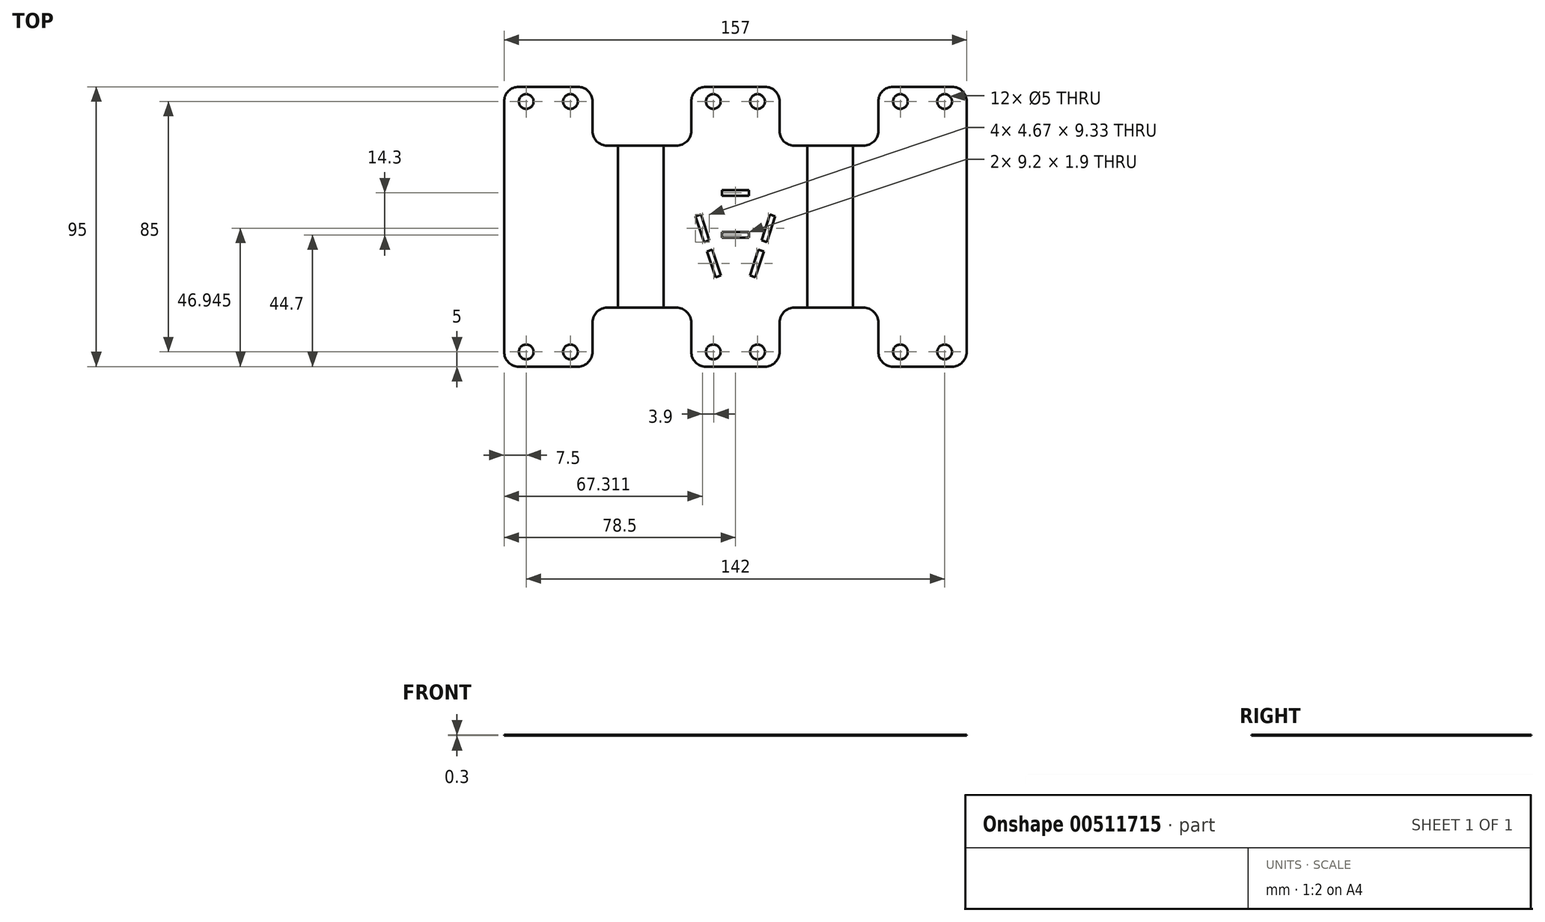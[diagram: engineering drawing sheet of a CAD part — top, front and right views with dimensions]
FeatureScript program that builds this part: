
annotation { "Feature Type Name" : "Feature", "Feature Type Description" : "" }
export const myFeature = defineFeature(function(context is Context, id is Id, definition is map)
    precondition{}
    {
        {
            var Q0;
            Q0=qCreatedBy(makeId("Top.planeOp"),FACE);
            var sketch = newSketch(context, id + "F0", { "sketchPlane" : qUnion([Q0])});
            skLineSegment(sketch, "E0.bottom", {"start": v(-15, 47.5) * mm, "end": v(15, 47.5) * mm});
            skLineSegment(sketch, "E0.top", {"start": v(-15, -47.5) * mm, "end": v(15, -47.5) * mm});
            skLineSegment(sketch, "E0.left", {"start": v(-15, 47.5) * mm, "end": v(-15, 27.5) * mm});
            skLineSegment(sketch, "E0.right", {"start": v(15, 47.5) * mm, "end": v(15, 27.5) * mm});
            skLineSegment(sketch, "E1.bottom", {"start": v(48.5, 47.5) * mm, "end": v(78.5, 47.5) * mm});
            skLineSegment(sketch, "E1.top", {"start": v(48.5, -47.5) * mm, "end": v(78.5, -47.5) * mm});
            skLineSegment(sketch, "E1.left", {"start": v(48.5, 47.5) * mm, "end": v(48.5, 27.5) * mm});
            skLineSegment(sketch, "E1.right", {"start": v(78.5, 47.5) * mm, "end": v(78.5, -47.5) * mm});
            skLineSegment(sketch, "E2.bottom", {"start": v(-48.5, 47.5) * mm, "end": v(-78.5, 47.5) * mm});
            skLineSegment(sketch, "E2.top", {"start": v(-48.5, -47.5) * mm, "end": v(-78.5, -47.5) * mm});
            skLineSegment(sketch, "E2.left", {"start": v(-48.5, 47.5) * mm, "end": v(-48.5, 27.5) * mm});
            skLineSegment(sketch, "E2.right", {"start": v(-78.5, 47.5) * mm, "end": v(-78.5, -47.5) * mm});
            skLineSegment(sketch, "E3.bottom", {"start": v(-48.5, 27.5) * mm, "end": v(-15, 27.5) * mm});
            skLineSegment(sketch, "E3.top", {"start": v(-48.5, -27.5) * mm, "end": v(-15, -27.5) * mm});
            skLineSegment(sketch, "E4.bottom", {"start": v(15, -27.5) * mm, "end": v(48.5, -27.5) * mm});
            skLineSegment(sketch, "E4.top", {"start": v(15, 27.5) * mm, "end": v(48.5, 27.5) * mm});
            skLineSegment(sketch, "E5.trimOffspring", {"start": v(-48.5, -27.5) * mm, "end": v(-48.5, -47.5) * mm});
            skLineSegment(sketch, "E6.trimOffspring", {"start": v(-15, -27.5) * mm, "end": v(-15, -47.5) * mm});
            skLineSegment(sketch, "E7.trimOffspring", {"start": v(15, -27.5) * mm, "end": v(15, -47.5) * mm});
            skLineSegment(sketch, "E8.trimOffspring", {"start": v(48.5, -27.5) * mm, "end": v(48.5, -47.5) * mm});
            skCircle(sketch, "E9", {"center": v(-7.5, 42.5) * mm, "radius": 2.5 * mm});
            skCircle(sketch, "E10", {"center": v(7.5, 42.5) * mm, "radius": 2.5 * mm});
            skCircle(sketch, "E11", {"center": v(-7.5, -42.5) * mm, "radius": 2.5 * mm});
            skCircle(sketch, "E12", {"center": v(7.5, -42.5) * mm, "radius": 2.5 * mm});
            skCircle(sketch, "E13", {"center": v(-56, 42.5) * mm, "radius": 2.5 * mm});
            skCircle(sketch, "E14", {"center": v(-71, 42.5) * mm, "radius": 2.5 * mm});
            skCircle(sketch, "E15", {"center": v(-56, -42.5) * mm, "radius": 2.5 * mm});
            skCircle(sketch, "E16", {"center": v(-71, -42.5) * mm, "radius": 2.5 * mm});
            skCircle(sketch, "E17", {"center": v(56, -42.5) * mm, "radius": 2.5 * mm});
            skCircle(sketch, "E18", {"center": v(71, -42.5) * mm, "radius": 2.5 * mm});
            skCircle(sketch, "E19", {"center": v(71, 42.5) * mm, "radius": 2.5 * mm});
            skCircle(sketch, "E20", {"center": v(56, 42.5) * mm, "radius": 2.5 * mm});
            skSolve(sketch);
        }
        {
            var Q0;
            Q0 = qSketchRegion(id + "F0", true);
            extrude(context, id + "F1", {"entities" : qUnion([Q0]), "depth" : 25 * mm});
        }
        {
            var Q0;
            Q0 = qSketchRegion(id + "F0", true);
            extrude(context, id + "F2", {"entities" : qUnion([Q0]), "operationType" : NewBodyOperationType.REMOVE, "oppositeDirection" : true, "depth" : 25 * mm});
        }
        {
            var Q0;
            Q0=makeQuery(id+"F1.opExtrude","CAP_FACE",FACE,{"disambiguationData":[OSD([sQuery(id+"F0.wireOp",EDGE,"E0.bottom"),sQuery(id+"F0.wireOp",EDGE,"E0.top"),sQuery(id+"F0.wireOp",EDGE,"E0.left"),sQuery(id+"F0.wireOp",EDGE,"E0.right"),sQuery(id+"F0.wireOp",EDGE,"E1.bottom"),sQuery(id+"F0.wireOp",EDGE,"E1.top"),sQuery(id+"F0.wireOp",EDGE,"E1.left"),sQuery(id+"F0.wireOp",EDGE,"E1.right"),sQuery(id+"F0.wireOp",EDGE,"E2.bottom"),sQuery(id+"F0.wireOp",EDGE,"E2.top"),sQuery(id+"F0.wireOp",EDGE,"E2.left"),sQuery(id+"F0.wireOp",EDGE,"E2.right"),sQuery(id+"F0.wireOp",EDGE,"E3.bottom"),sQuery(id+"F0.wireOp",EDGE,"E3.top"),sQuery(id+"F0.wireOp",EDGE,"E4.bottom"),sQuery(id+"F0.wireOp",EDGE,"E4.top"),sQuery(id+"F0.wireOp",EDGE,"E5.trimOffspring"),sQuery(id+"F0.wireOp",EDGE,"E6.trimOffspring"),sQuery(id+"F0.wireOp",EDGE,"E7.trimOffspring"),sQuery(id+"F0.wireOp",EDGE,"E8.trimOffspring"),sQuery(id+"F0.wireOp",EDGE,"E9"),sQuery(id+"F0.wireOp",EDGE,"E10"),sQuery(id+"F0.wireOp",EDGE,"E11"),sQuery(id+"F0.wireOp",EDGE,"E12"),sQuery(id+"F0.wireOp",EDGE,"E13"),sQuery(id+"F0.wireOp",EDGE,"E14"),sQuery(id+"F0.wireOp",EDGE,"E15"),sQuery(id+"F0.wireOp",EDGE,"E16"),sQuery(id+"F0.wireOp",EDGE,"E17"),sQuery(id+"F0.wireOp",EDGE,"E18"),sQuery(id+"F0.wireOp",EDGE,"E19"),sQuery(id+"F0.wireOp",EDGE,"E20")])],"isStart":false});
            var sketch = newSketch(context, id + "F3", { "sketchPlane" : qUnion([Q0])});
            skLineSegment(sketch, "E21.bottom", {"start": v(-4.6, 12.45) * mm, "end": v(4.6, 12.45) * mm});
            skLineSegment(sketch, "E21.top", {"start": v(-4.6, 10.55) * mm, "end": v(4.6, 10.55) * mm});
            skLineSegment(sketch, "E21.left", {"start": v(-4.6, 12.45) * mm, "end": v(-4.6, 10.55) * mm});
            skLineSegment(sketch, "E21.right", {"start": v(4.6, 12.45) * mm, "end": v(4.6, 10.55) * mm});
            skLineSegment(sketch, "E22.bottom", {"start": v(-4.6, -3.75) * mm, "end": v(4.6, -3.75) * mm});
            skLineSegment(sketch, "E22.top", {"start": v(-4.6, -1.85) * mm, "end": v(4.6, -1.85) * mm});
            skLineSegment(sketch, "E22.left", {"start": v(-4.6, -3.75) * mm, "end": v(-4.6, -1.85) * mm});
            skLineSegment(sketch, "E22.right", {"start": v(4.6, -3.75) * mm, "end": v(4.6, -1.85) * mm});
            skLineSegment(sketch, "E23", {"start": v(-11.72, 4.11) * mm, "end": v(-8.85, -4.63) * mm});
            skLineSegment(sketch, "E24", {"start": v(-4.95, -16.53) * mm, "end": v(-6.76, -17.12) * mm});
            skLineSegment(sketch, "E25", {"start": v(-6.76, -17.12) * mm, "end": v(-9.62, -8.38) * mm});
            skLineSegment(sketch, "E26", {"start": v(-13.52, 3.52) * mm, "end": v(-11.72, 4.11) * mm});
            skLineSegment(sketch, "E27", {"start": v(11.72, 4.11) * mm, "end": v(8.85, -4.63) * mm});
            skLineSegment(sketch, "E28", {"start": v(4.95, -16.53) * mm, "end": v(6.76, -17.12) * mm});
            skLineSegment(sketch, "E29", {"start": v(6.76, -17.12) * mm, "end": v(9.62, -8.38) * mm});
            skLineSegment(sketch, "E30", {"start": v(13.52, 3.52) * mm, "end": v(11.72, 4.11) * mm});
            skLineSegment(sketch, "E31", {"start": v(-10.66, -5.22) * mm, "end": v(-8.85, -4.63) * mm});
            skLineSegment(sketch, "E32", {"start": v(-9.62, -8.38) * mm, "end": v(-7.82, -7.79) * mm});
            skLineSegment(sketch, "E33", {"start": v(8.85, -4.63) * mm, "end": v(10.66, -5.22) * mm});
            skLineSegment(sketch, "E34", {"start": v(7.82, -7.79) * mm, "end": v(9.62, -8.38) * mm});
            skLineSegment(sketch, "E35.trimOffspring", {"start": v(10.66, -5.22) * mm, "end": v(13.52, 3.52) * mm});
            skLineSegment(sketch, "E36.trimOffspring", {"start": v(7.82, -7.79) * mm, "end": v(4.95, -16.53) * mm});
            skLineSegment(sketch, "E37.trimOffspring", {"start": v(-7.82, -7.79) * mm, "end": v(-4.95, -16.53) * mm});
            skLineSegment(sketch, "E38.trimOffspring", {"start": v(-10.66, -5.22) * mm, "end": v(-13.52, 3.52) * mm});
            skSolve(sketch);
        }
        {
            var Q0;
            Q0 = qSketchRegion(id + "F3", true);
            extrude(context, id + "F4", {"entities" : qUnion([Q0]), "operationType" : NewBodyOperationType.REMOVE, "oppositeDirection" : true, "depth" : 25 * mm});
        }
        {
            var Q0;
            Q0=makeQuery(id+"F1.opExtrude","SWEPT_EDGE",EDGE,{"disambiguationData":[OSD([sQuery(id+"F0.wireOp",EDGE,"E2.bottom"),sQuery(id+"F0.wireOp",EDGE,"E2.left")])]});
            var Q1;
            Q1=makeQuery(id+"F1.opExtrude","SWEPT_EDGE",EDGE,{"disambiguationData":[OSD([sQuery(id+"F0.wireOp",EDGE,"E2.left"),sQuery(id+"F0.wireOp",EDGE,"E3.bottom")])]});
            var Q2;
            Q2=makeQuery(id+"F1.opExtrude","SWEPT_EDGE",EDGE,{"disambiguationData":[OSD([sQuery(id+"F0.wireOp",EDGE,"E0.bottom"),sQuery(id+"F0.wireOp",EDGE,"E0.right")])]});
            var Q3;
            Q3=makeQuery(id+"F1.opExtrude","SWEPT_EDGE",EDGE,{"disambiguationData":[OSD([sQuery(id+"F0.wireOp",EDGE,"E0.right"),sQuery(id+"F0.wireOp",EDGE,"E4.top")])]});
            var Q4;
            Q4=makeQuery(id+"F1.opExtrude","SWEPT_EDGE",EDGE,{"disambiguationData":[OSD([sQuery(id+"F0.wireOp",EDGE,"E1.bottom"),sQuery(id+"F0.wireOp",EDGE,"E1.right")])]});
            var Q5;
            Q5=makeQuery(id+"F1.opExtrude","SWEPT_EDGE",EDGE,{"disambiguationData":[OSD([sQuery(id+"F0.wireOp",EDGE,"E1.bottom"),sQuery(id+"F0.wireOp",EDGE,"E1.left")])]});
            var Q6;
            Q6=makeQuery(id+"F1.opExtrude","SWEPT_EDGE",EDGE,{"disambiguationData":[OSD([sQuery(id+"F0.wireOp",EDGE,"E0.bottom"),sQuery(id+"F0.wireOp",EDGE,"E0.left")])]});
            var Q7;
            Q7=makeQuery(id+"F1.opExtrude","SWEPT_EDGE",EDGE,{"disambiguationData":[OSD([sQuery(id+"F0.wireOp",EDGE,"E1.left"),sQuery(id+"F0.wireOp",EDGE,"E4.top")])]});
            var Q8;
            Q8=makeQuery(id+"F1.opExtrude","SWEPT_EDGE",EDGE,{"disambiguationData":[OSD([sQuery(id+"F0.wireOp",EDGE,"E0.left"),sQuery(id+"F0.wireOp",EDGE,"E3.bottom")])]});
            var Q9;
            Q9=makeQuery(id+"F1.opExtrude","SWEPT_EDGE",EDGE,{"disambiguationData":[OSD([sQuery(id+"F0.wireOp",EDGE,"E2.bottom"),sQuery(id+"F0.wireOp",EDGE,"E2.right")])]});
            var Q10;
            Q10=makeQuery(id+"F1.opExtrude","SWEPT_EDGE",EDGE,{"disambiguationData":[OSD([sQuery(id+"F0.wireOp",EDGE,"E4.bottom"),sQuery(id+"F0.wireOp",EDGE,"E7.trimOffspring")])]});
            var Q11;
            Q11=makeQuery(id+"F1.opExtrude","SWEPT_EDGE",EDGE,{"disambiguationData":[OSD([sQuery(id+"F0.wireOp",EDGE,"E0.top"),sQuery(id+"F0.wireOp",EDGE,"E7.trimOffspring")])]});
            var Q12;
            Q12=makeQuery(id+"F1.opExtrude","SWEPT_EDGE",EDGE,{"disambiguationData":[OSD([sQuery(id+"F0.wireOp",EDGE,"E1.top"),sQuery(id+"F0.wireOp",EDGE,"E1.right")])]});
            var Q13;
            Q13=makeQuery(id+"F1.opExtrude","SWEPT_EDGE",EDGE,{"disambiguationData":[OSD([sQuery(id+"F0.wireOp",EDGE,"E3.top"),sQuery(id+"F0.wireOp",EDGE,"E5.trimOffspring")])]});
            var Q14;
            Q14=makeQuery(id+"F1.opExtrude","SWEPT_EDGE",EDGE,{"disambiguationData":[OSD([sQuery(id+"F0.wireOp",EDGE,"E2.top"),sQuery(id+"F0.wireOp",EDGE,"E5.trimOffspring")])]});
            var Q15;
            Q15=makeQuery(id+"F1.opExtrude","SWEPT_EDGE",EDGE,{"disambiguationData":[OSD([sQuery(id+"F0.wireOp",EDGE,"E4.bottom"),sQuery(id+"F0.wireOp",EDGE,"E8.trimOffspring")])]});
            var Q16;
            Q16=makeQuery(id+"F1.opExtrude","SWEPT_EDGE",EDGE,{"disambiguationData":[OSD([sQuery(id+"F0.wireOp",EDGE,"E1.top"),sQuery(id+"F0.wireOp",EDGE,"E8.trimOffspring")])]});
            var Q17;
            Q17=makeQuery(id+"F1.opExtrude","SWEPT_EDGE",EDGE,{"disambiguationData":[OSD([sQuery(id+"F0.wireOp",EDGE,"E3.top"),sQuery(id+"F0.wireOp",EDGE,"E6.trimOffspring")])]});
            var Q18;
            Q18=makeQuery(id+"F1.opExtrude","SWEPT_EDGE",EDGE,{"disambiguationData":[OSD([sQuery(id+"F0.wireOp",EDGE,"E0.top"),sQuery(id+"F0.wireOp",EDGE,"E6.trimOffspring")])]});
            var Q19;
            Q19=makeQuery(id+"F1.opExtrude","SWEPT_EDGE",EDGE,{"disambiguationData":[OSD([sQuery(id+"F0.wireOp",EDGE,"E2.top"),sQuery(id+"F0.wireOp",EDGE,"E2.right")])]});
            fillet(context, id + "F5", {"entities" : qUnion([Q0, Q1, Q2, Q3, Q4, Q5, Q6, Q7, Q8, Q9, Q10, Q11, Q12, Q13, Q14, Q15, Q16, Q17, Q18, Q19]), "radius" : 5 * mm, "tangentPropagation" : true, "allowEdgeOverflow" : false});
        }
        {
            var Q0;
            Q0=qCreatedBy(makeId("Front.planeOp"),FACE);
            var sketch = newSketch(context, id + "F6", { "sketchPlane" : qUnion([Q0])});
            skLineSegment(sketch, "E39", {"start": v(-40.85, 32.5) * mm, "end": v(-38.85, 32.5) * mm});
            skLineSegment(sketch, "E40", {"start": v(-40.85, 32.5) * mm, "end": v(-39.85, 24.9) * mm});
            skLineSegment(sketch, "E41", {"start": v(-39.85, 24.9) * mm, "end": v(-38.85, 32.5) * mm});
            skLineSegment(sketch, "E42", {"start": v(-25.35, 32.5) * mm, "end": v(-24.35, 24.9) * mm});
            skLineSegment(sketch, "E43", {"start": v(-24.35, 24.9) * mm, "end": v(-23.35, 32.5) * mm});
            skLineSegment(sketch, "E44", {"start": v(40.85, 32.5) * mm, "end": v(39.85, 24.9) * mm});
            skLineSegment(sketch, "E45", {"start": v(39.85, 24.9) * mm, "end": v(38.85, 32.5) * mm});
            skLineSegment(sketch, "E46", {"start": v(25.35, 32.5) * mm, "end": v(24.35, 24.9) * mm});
            skLineSegment(sketch, "E47", {"start": v(24.35, 24.9) * mm, "end": v(23.35, 32.5) * mm});
            skLineSegment(sketch, "E48.trimOffspring", {"start": v(-25.35, 32.5) * mm, "end": v(-23.35, 32.5) * mm});
            skLineSegment(sketch, "E49.trimOffspring", {"start": v(23.35, 32.5) * mm, "end": v(25.35, 32.5) * mm});
            skLineSegment(sketch, "E50.trimOffspring", {"start": v(38.85, 32.5) * mm, "end": v(40.85, 32.5) * mm});
            skSolve(sketch);
        }
        {
            var Q0;
            {var subQ0=sQuery(id+"F6.wireOp",EDGE,"E40");Q0=makeQuery(id+"F6.imprint","IMPRINT",FACE,{"disambiguationData":[TD([[makeQuery(id+"F6.imprint","IMPRINT",EDGE,{"derivedFrom":subQ0}),1.0]])]});}
            var Q1;
            {var subQ0=sQuery(id+"F6.wireOp",EDGE,"E44");Q1=makeQuery(id+"F6.imprint","IMPRINT",FACE,{"disambiguationData":[TD([[makeQuery(id+"F6.imprint","IMPRINT",EDGE,{"derivedFrom":subQ0}),-1.0]])]});}
            var Q2;
            {var subQ0=sQuery(id+"F6.wireOp",EDGE,"E42");Q2=makeQuery(id+"F6.imprint","IMPRINT",FACE,{"disambiguationData":[TD([[makeQuery(id+"F6.imprint","IMPRINT",EDGE,{"derivedFrom":subQ0}),1.0]])]});}
            var Q3;
            {var subQ0=sQuery(id+"F6.wireOp",EDGE,"E46");Q3=makeQuery(id+"F6.imprint","IMPRINT",FACE,{"disambiguationData":[TD([[makeQuery(id+"F6.imprint","IMPRINT",EDGE,{"derivedFrom":subQ0}),-1.0]])]});}
            extrude(context, id + "F7", {"entities" : qUnion([Q0, Q1, Q2, Q3]), "operationType" : NewBodyOperationType.REMOVE, "oppositeDirection" : true, "depth" : 80 * mm, "symmetric" : true});
        }
        {
            var Q0;
            Q0=makeQuery(id+"F1.opExtrude","SWEPT_FACE",FACE,{"disambiguationData":[OSD([sQuery(id+"F0.wireOp",EDGE,"E0.top")])]});
            var sketch = newSketch(context, id + "F8", { "sketchPlane" : qUnion([Q0])});
            skLineSegment(sketch, "E51.bottom", {"start": v(-80, 24.7) * mm, "end": v(85.97, 24.7) * mm});
            skLineSegment(sketch, "E51.top", {"start": v(-80, -7.88) * mm, "end": v(85.97, -7.88) * mm});
            skLineSegment(sketch, "E51.left", {"start": v(-80, 24.7) * mm, "end": v(-80, -7.88) * mm});
            skLineSegment(sketch, "E51.right", {"start": v(85.97, 24.7) * mm, "end": v(85.97, -7.88) * mm});
            skSolve(sketch);
        }
        {
            var Q0;
            Q0 = qSketchRegion(id + "F8", true);
            extrude(context, id + "F9", {"entities" : qUnion([Q0]), "operationType" : NewBodyOperationType.REMOVE, "oppositeDirection" : true, "depth" : 97 * mm});
        }
    });
